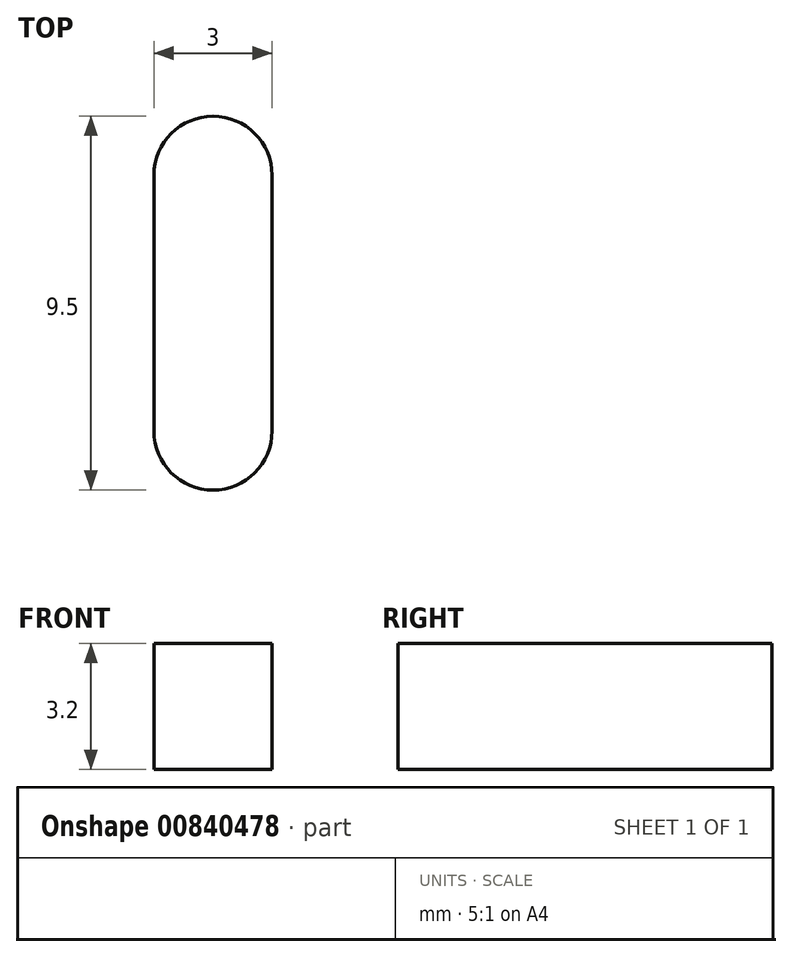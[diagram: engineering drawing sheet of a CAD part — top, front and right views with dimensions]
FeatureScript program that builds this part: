
annotation { "Feature Type Name" : "Feature", "Feature Type Description" : "" }
export const myFeature = defineFeature(function(context is Context, id is Id, definition is map)
    precondition{}
    {
        {
            var Q0;
            Q0=qCreatedBy(makeId("Top.planeOp"),FACE);
            var sketch = newSketch(context, id + "F0", { "sketchPlane" : qUnion([Q0])});
            skArc(sketch, "E0", {"start": v(1.45, 3.5) * mm, "mid": v(-0.05, 5) * mm, "end": v(-1.55, 3.5) * mm});
            skArc(sketch, "E1", {"start": v(-1.55, -3) * mm, "mid": v(-0.05, -4.5) * mm, "end": v(1.45, -3) * mm});
            skLineSegment(sketch, "E2", {"start": v(-1.55, 3.5) * mm, "end": v(-1.55, -3) * mm});
            skLineSegment(sketch, "E3", {"start": v(1.45, 3.5) * mm, "end": v(1.45, -3) * mm});
            skLineSegment(sketch, "E4.0", {"start": v(4.95, 10.5) * mm, "end": v(-5.05, 10.5) * mm});
            skLineSegment(sketch, "E5.0", {"start": v(-5.05, -11.5) * mm, "end": v(4.95, -11.5) * mm});
            skSolve(sketch);
        }
        {
            var Q0;
            Q0=makeQuery(id+"F0.imprint","IMPRINT",FACE,{"disambiguationData":[TD([[makeQuery(id+"F0.imprint","IMPRINT",EDGE,{"derivedFrom":sQuery(id+"F0.wireOp",EDGE,"E0")}),1.0]])]});
            extrude(context, id + "F1", {"entities" : qUnion([Q0]), "depth" : (1.8 + 1.4) * mm, "offsetDistance" : 25 * mm});
        }
    });
